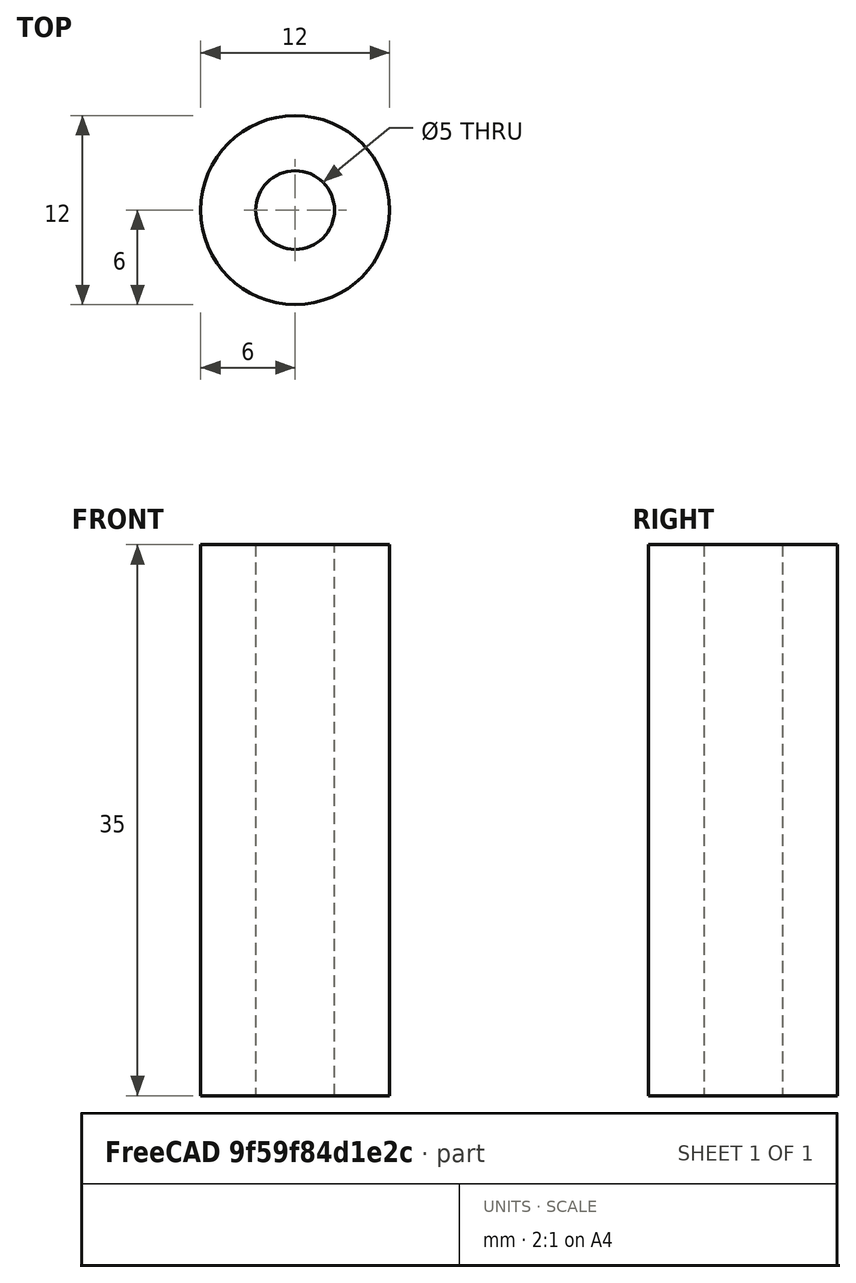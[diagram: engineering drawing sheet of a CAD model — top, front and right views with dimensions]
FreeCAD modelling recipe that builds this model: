
FCSTD DOCUMENT  (FreeCAD 0.20R29410 (Git))
Label: #2_BaseSpacers
License: All rights reserved
LicenseURL: http://en.wikipedia.org/wiki/All_rights_reserved
objects: Sketcher::SketchObject×1, PartDesign::Pad×1, PartDesign::Body×1
note: 4 computed .brp shape members not serialized (recipe doc carries the construction recipe); baked Part::Feature solids carry a one-line shape summary decoded from their .brp

FEATURE [Sketcher::SketchObject] Sketch
  FullyConstrained = true
  MapMode = 5
  Support = -> [XY_Plane]
  sketch-geometry (2):
    g0: Circle CenterX=0 CenterY=0 CenterZ=0 NormalX=0 NormalY=0 NormalZ=1 AngleXU=0 Radius=6
    g1: Circle CenterX=0 CenterY=0 CenterZ=0 NormalX=0 NormalY=0 NormalZ=1 AngleXU=0 Radius=2.5
  constraints (4):
    c: Coincident(g0,g-1)
    c: Coincident(g1,g0)
    c: Diameter(g1) = 5
    c: Diameter(g0) = 12
FEATURE [PartDesign::Pad] Pad
  Direction = (0,0,1)
  Length = 35
  Length2 = 10
  Profile = -> Sketch
  ReferenceAxis = -> Sketch [N_Axis]
  Type = 0
FEATURE [PartDesign::Body] Body
  Group = -> [Sketch,Pad]
  Origin = -> Origin
  Tip = -> Pad
